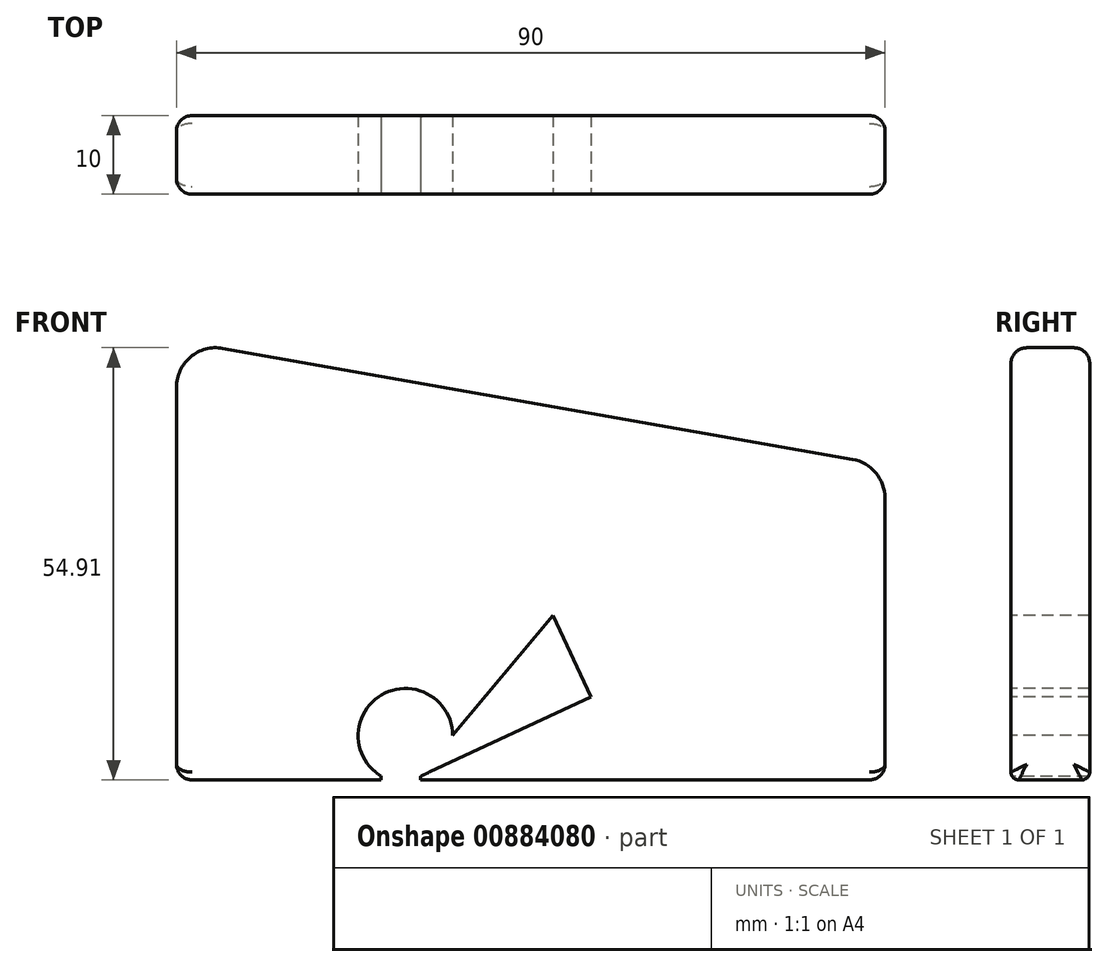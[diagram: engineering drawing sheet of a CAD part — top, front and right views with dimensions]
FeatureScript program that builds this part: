
annotation { "Feature Type Name" : "Feature", "Feature Type Description" : "" }
export const myFeature = defineFeature(function(context is Context, id is Id, definition is map)
    precondition{}
    {
        {
            var Q0;
            Q0=qCreatedBy(makeId("Front.planeOp"),FACE);
            var sketch = newSketch(context, id + "F0", { "sketchPlane" : qUnion([Q0])});
            skLineSegment(sketch, "E0", {"start": v(-45, 0) * mm, "end": v(45, 0) * mm});
            skLineSegment(sketch, "E1", {"start": v(45, 0) * mm, "end": v(45, 40) * mm});
            skLineSegment(sketch, "E2", {"start": v(45, 40) * mm, "end": v(-45, 55.87) * mm});
            skLineSegment(sketch, "E3", {"start": v(-45, 55.87) * mm, "end": v(-45, 0) * mm});
            skSolve(sketch);
        }
        {
            var Q0;
            Q0=makeQuery(id+"F0.imprint","IMPRINT",FACE,{"disambiguationData":[TD([[makeQuery(id+"F0.imprint","IMPRINT",EDGE,{"derivedFrom":sQuery(id+"F0.wireOp",EDGE,"E0")}),1.0]])]});
            extrude(context, id + "F1", {"entities" : qUnion([Q0]), "depth" : 10 * mm, "offsetDistance" : 25 * mm});
        }
        {
            var Q0;
            Q0=makeQuery(id+"F1.opExtrude","CAP_FACE",FACE,{"disambiguationData":[OSD([sQuery(id+"F0.wireOp",EDGE,"E0"),sQuery(id+"F0.wireOp",EDGE,"E1"),sQuery(id+"F0.wireOp",EDGE,"E2"),sQuery(id+"F0.wireOp",EDGE,"E3")])],"isStart":false});
            var sketch = newSketch(context, id + "F2", { "sketchPlane" : qUnion([Q0])});
            skLineSegment(sketch, "E4", {"start": v(-14, 0.47) * mm, "end": v(7.66, 10.57) * mm});
            skLineSegment(sketch, "E5", {"start": v(7.66, 10.57) * mm, "end": v(2.84, 20.9) * mm});
            skLineSegment(sketch, "E6", {"start": v(2.84, 20.9) * mm, "end": v(-9.92, 5.68) * mm});
            skLineSegment(sketch, "E7", {"start": v(-18, 0) * mm, "end": v(-15, 0) * mm});
            skLineSegment(sketch, "E8", {"start": v(-9.92, 5.68) * mm, "end": v(-8.66, 2.96) * mm, "construction": true});
            skArc(sketch, "E9", {"start": v(-9.92, 5.68) * mm, "mid": v(-18.9, 10.84) * mm, "end": v(-19, 0.48) * mm});
            skLineSegment(sketch, "E10", {"start": v(-14, 0.47) * mm, "end": v(-14, 0) * mm});
            skLineSegment(sketch, "E11", {"start": v(-14, 0) * mm, "end": v(-15, 0) * mm});
            skLineSegment(sketch, "E12", {"start": v(-19, 0.48) * mm, "end": v(-19, 0) * mm});
            skLineSegment(sketch, "E13", {"start": v(-19, 0) * mm, "end": v(-18, 0) * mm});
            skSolve(sketch);
        }
        {
            var Q0;
            Q0=makeQuery(id+"F2.imprint","IMPRINT",FACE,{"disambiguationData":[TD([[makeQuery(id+"F2.imprint","IMPRINT",EDGE,{"derivedFrom":sQuery(id+"F2.wireOp",EDGE,"E4")}),1.0]])]});
            extrude(context, id + "F3", {"entities" : qUnion([Q0]), "operationType" : NewBodyOperationType.REMOVE, "endBound" : BoundingType.UP_TO_NEXT, "oppositeDirection" : true, "depth" : 31.3 * mm, "offsetDistance" : 25 * mm});
        }
        {
            var Q0;
            Q0=makeQuery(id+"F1.opExtrude","SWEPT_EDGE",EDGE,{"disambiguationData":[OSD([sQuery(id+"F0.wireOp",EDGE,"E2"),sQuery(id+"F0.wireOp",EDGE,"E3")])]});
            var Q1;
            Q1=makeQuery(id+"F1.opExtrude","SWEPT_EDGE",EDGE,{"disambiguationData":[OSD([sQuery(id+"F0.wireOp",EDGE,"E1"),sQuery(id+"F0.wireOp",EDGE,"E2")])]});
            fillet(context, id + "F4", {"entities" : qUnion([Q0, Q1]), "radius" : 5 * mm, "tangentPropagation" : true, "allowEdgeOverflow" : false});
        }
        {
            var Q0;
            Q0=makeQuery(id+"F1.opExtrude","SWEPT_EDGE",EDGE,{"disambiguationData":[OSD([sQuery(id+"F0.wireOp",EDGE,"E0"),sQuery(id+"F0.wireOp",EDGE,"E3")])]});
            var Q1;
            Q1=makeQuery(id+"F1.opExtrude","SWEPT_EDGE",EDGE,{"disambiguationData":[OSD([sQuery(id+"F0.wireOp",EDGE,"E0"),sQuery(id+"F0.wireOp",EDGE,"E1")])]});
            var Q2;
            Q2=makeQuery(id+"F1.opExtrude","CAP_EDGE",EDGE,{"disambiguationData":[OSD([sQuery(id+"F0.wireOp",EDGE,"E3")])],"isStart":false});
            var Q3;
            Q3=makeQuery(id+"F1.opExtrude","CAP_EDGE",EDGE,{"disambiguationData":[OSD([sQuery(id+"F0.wireOp",EDGE,"E3")])],"isStart":true});
            fillet(context, id + "F5", {"entities" : qUnion([Q0, Q1, Q2, Q3]), "radius" : 2 * mm, "tangentPropagation" : true, "allowEdgeOverflow" : false});
        }
        {
            var Q0;
            {var subQ0=sQuery(id+"F0.wireOp",EDGE,"E0");var subQ1=sQuery(id+"F0.wireOp",EDGE,"E3");Q0=makeQuery(id+"F3.boolean.opBoolean","SPLIT",EDGE,{"disambiguationData":[TD([makeQuery(id+"F1.opExtrude","SWEPT_FACE",FACE,{"disambiguationData":[OSD([subQ1])]})])],"derivedFrom":makeQuery(id+"F1.opExtrude","CAP_EDGE",EDGE,{"disambiguationData":[OSD([subQ0])],"isStart":false})});}
            var Q1;
            {var subQ0=sQuery(id+"F0.wireOp",EDGE,"E0");var subQ1=sQuery(id+"F0.wireOp",EDGE,"E1");Q1=makeQuery(id+"F3.boolean.opBoolean","SPLIT",EDGE,{"disambiguationData":[TD([makeQuery(id+"F1.opExtrude","SWEPT_FACE",FACE,{"disambiguationData":[OSD([subQ1])]})])],"derivedFrom":makeQuery(id+"F1.opExtrude","CAP_EDGE",EDGE,{"disambiguationData":[OSD([subQ0])],"isStart":false})});}
            var Q2;
            {var subQ0=sQuery(id+"F0.wireOp",EDGE,"E0");var subQ1=sQuery(id+"F0.wireOp",EDGE,"E1");Q2=makeQuery(id+"F3.boolean.opBoolean","SPLIT",EDGE,{"disambiguationData":[TD([makeQuery(id+"F1.opExtrude","SWEPT_FACE",FACE,{"disambiguationData":[OSD([subQ1])]})])],"derivedFrom":makeQuery(id+"F1.opExtrude","CAP_EDGE",EDGE,{"disambiguationData":[OSD([subQ0])],"isStart":true})});}
            var Q3;
            {var subQ0=sQuery(id+"F0.wireOp",EDGE,"E0");var subQ1=sQuery(id+"F0.wireOp",EDGE,"E3");Q3=makeQuery(id+"F3.boolean.opBoolean","SPLIT",EDGE,{"disambiguationData":[TD([makeQuery(id+"F1.opExtrude","SWEPT_FACE",FACE,{"disambiguationData":[OSD([subQ1])]})])],"derivedFrom":makeQuery(id+"F1.opExtrude","CAP_EDGE",EDGE,{"disambiguationData":[OSD([subQ0])],"isStart":true})});}
            fillet(context, id + "F6", {"entities" : qUnion([Q0, Q1, Q2, Q3]), "radius" : 1 * mm, "tangentPropagation" : true, "allowEdgeOverflow" : false});
        }
    });
